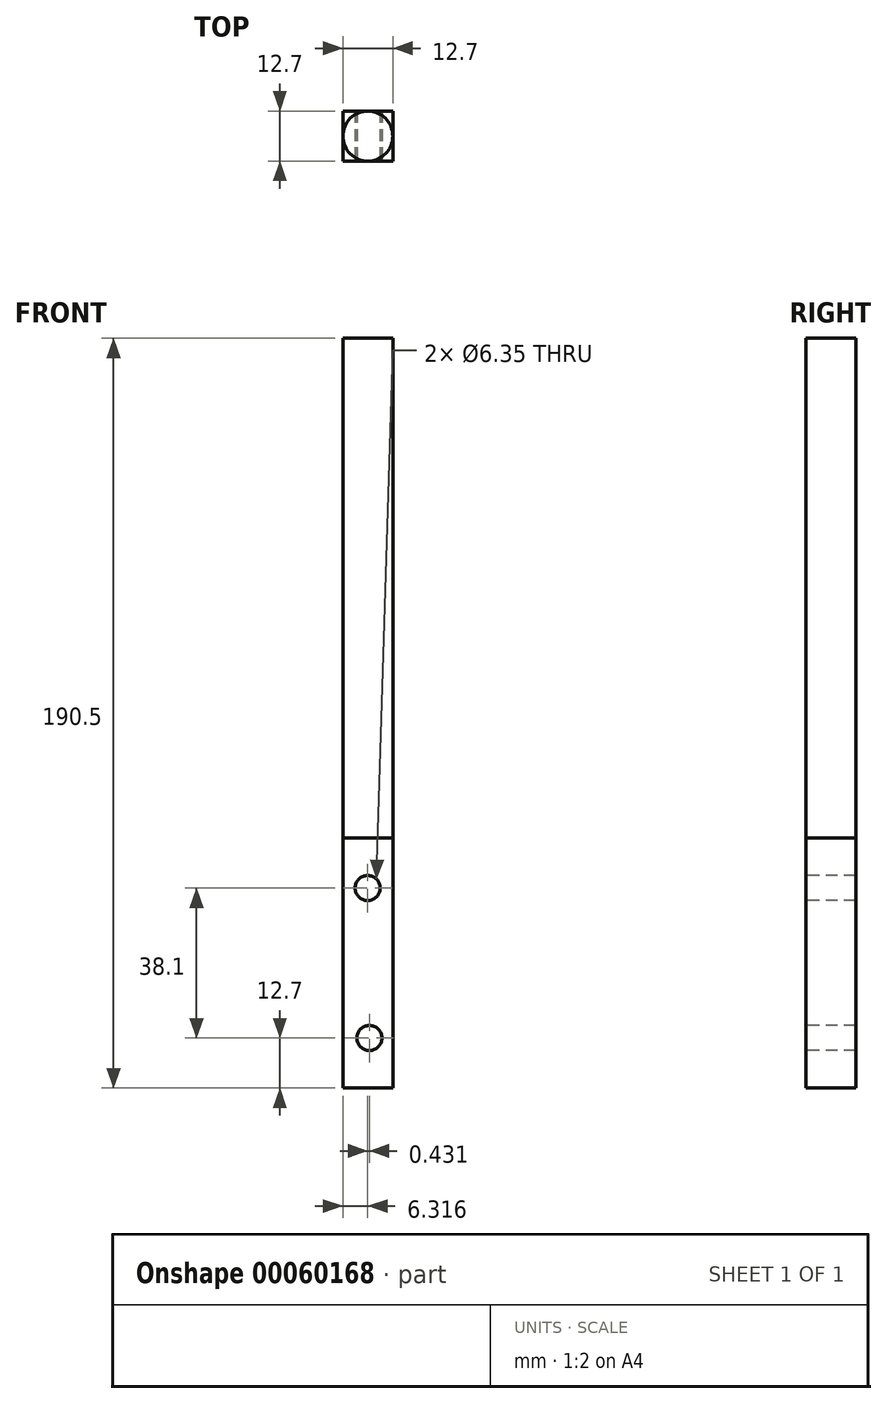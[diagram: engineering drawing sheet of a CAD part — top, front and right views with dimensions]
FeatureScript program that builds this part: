
annotation { "Feature Type Name" : "Feature", "Feature Type Description" : "" }
export const myFeature = defineFeature(function(context is Context, id is Id, definition is map)
    precondition{}
    {
        {
            var Q0;
            Q0=qCreatedBy(makeId("Top.planeOp"),FACE);
            var sketch = newSketch(context, id + "F0", { "sketchPlane" : qUnion([Q0])});
            skLineSegment(sketch, "E0.bottom", {"start": v(-4.52, 2.21) * mm, "end": v(8.18, 2.21) * mm});
            skLineSegment(sketch, "E0.top", {"start": v(-4.52, -10.49) * mm, "end": v(8.18, -10.49) * mm});
            skLineSegment(sketch, "E0.left", {"start": v(-4.52, 2.21) * mm, "end": v(-4.52, -10.49) * mm});
            skLineSegment(sketch, "E0.right", {"start": v(8.18, 2.21) * mm, "end": v(8.18, -10.49) * mm});
            skSolve(sketch);
        }
        {
            var Q0;
            Q0 = qSketchRegion(id + "F0", true);
            extrude(context, id + "F1", {"entities" : qUnion([Q0]), "depth" : 63.5 * mm});
        }
        {
            var Q0;
            Q0=makeQuery(id+"F1.opExtrude","CAP_FACE",FACE,{"disambiguationData":[OSD([sQuery(id+"F0.wireOp",EDGE,"E0.bottom"),sQuery(id+"F0.wireOp",EDGE,"E0.top"),sQuery(id+"F0.wireOp",EDGE,"E0.left"),sQuery(id+"F0.wireOp",EDGE,"E0.right")])],"isStart":false});
            var sketch = newSketch(context, id + "F2", { "sketchPlane" : qUnion([Q0])});
            skCircle(sketch, "E1", {"center": v(1.83, -4.14) * mm, "radius": 6.35 * mm});
            skPoint(sketch, "E1.centerSnap0", {"position": v(1.83, 2.21) * mm});
            skPoint(sketch, "E1.centerSnap1", {"position": v(8.18, -4.14) * mm});
            skSolve(sketch);
        }
        {
            var Q0;
            Q0 = qSketchRegion(id + "F2", true);
            extrude(context, id + "F3", {"entities" : qUnion([Q0]), "operationType" : NewBodyOperationType.ADD, "depth" : 127 * mm});
        }
        {
            var Q0;
            Q0=makeQuery(id+"F1.opExtrude","SWEPT_FACE",FACE,{"disambiguationData":[OSD([sQuery(id+"F0.wireOp",EDGE,"E0.top")])]});
            var sketch = newSketch(context, id + "F4", { "sketchPlane" : qUnion([Q0])});
            skCircle(sketch, "E2", {"center": v(2.23, 12.7) * mm, "radius": 3.18 * mm});
            skCircle(sketch, "E3", {"center": v(1.8, 50.8) * mm, "radius": 3.18 * mm});
            skSolve(sketch);
        }
        {
            var Q0;
            Q0 = qSketchRegion(id + "F4", true);
            extrude(context, id + "F5", {"entities" : qUnion([Q0]), "operationType" : NewBodyOperationType.REMOVE, "oppositeDirection" : true, "depth" : 12.7 * mm});
        }
    });
